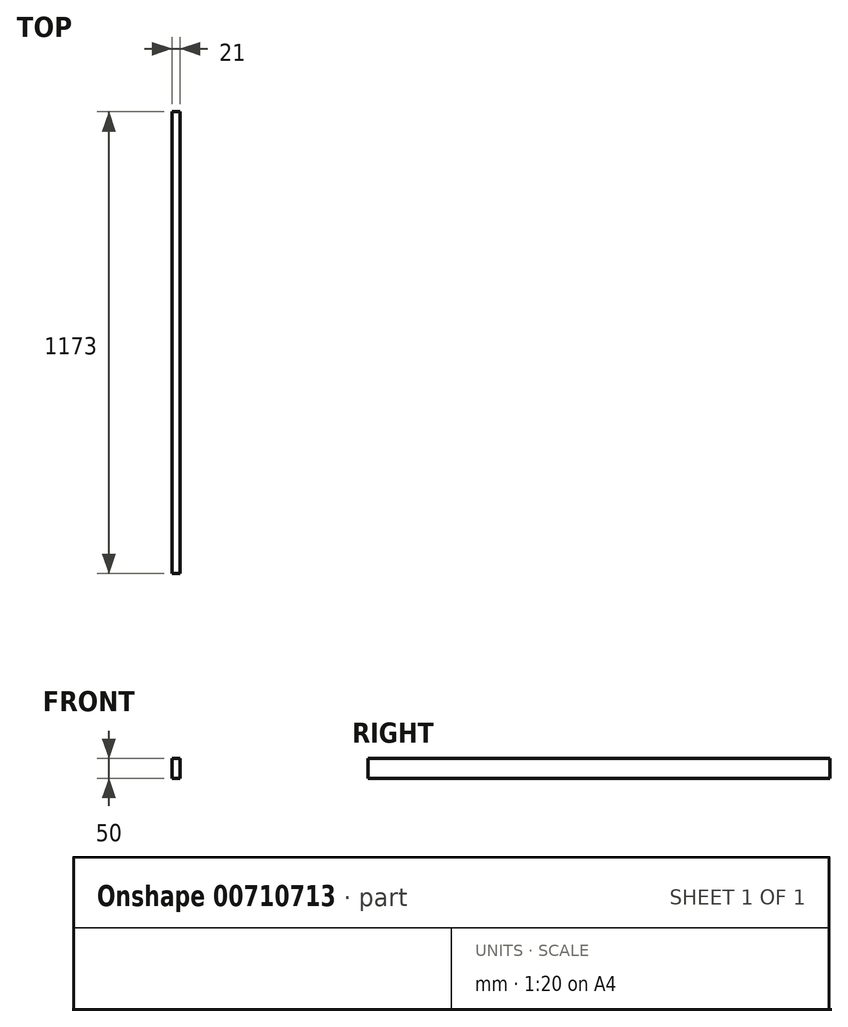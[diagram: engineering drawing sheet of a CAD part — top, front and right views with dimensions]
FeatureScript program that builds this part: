
annotation { "Feature Type Name" : "Feature", "Feature Type Description" : "" }
export const myFeature = defineFeature(function(context is Context, id is Id, definition is map)
    precondition{}
    {
        {
            assignVariable(context, id + "F0", {"name" : "l", "anyValue" : 1215 - 42});
        }
        {
            var Q0;
            Q0=qCreatedBy(makeId("Front.planeOp"),FACE);
            var sketch = newSketch(context, id + "F1", { "sketchPlane" : qUnion([Q0])});
            skLineSegment(sketch, "E0.bottom", {"start": v(0, 0) * mm, "end": v(21, 0) * mm});
            skLineSegment(sketch, "E0.top", {"start": v(0, 50) * mm, "end": v(21, 50) * mm});
            skLineSegment(sketch, "E0.left", {"start": v(0, 0) * mm, "end": v(0, 50) * mm});
            skLineSegment(sketch, "E0.right", {"start": v(21, 0) * mm, "end": v(21, 50) * mm});
            skSolve(sketch);
        }
        {
            var Q0;
            Q0=qSketchRegion(id+"F1",true);
            extrude(context, id + "F2", {"entities" : qUnion([Q0]), "depth" : (getVariable(context, 'l')) * mm, "offsetDistance" : 25 * mm});
        }
    });
